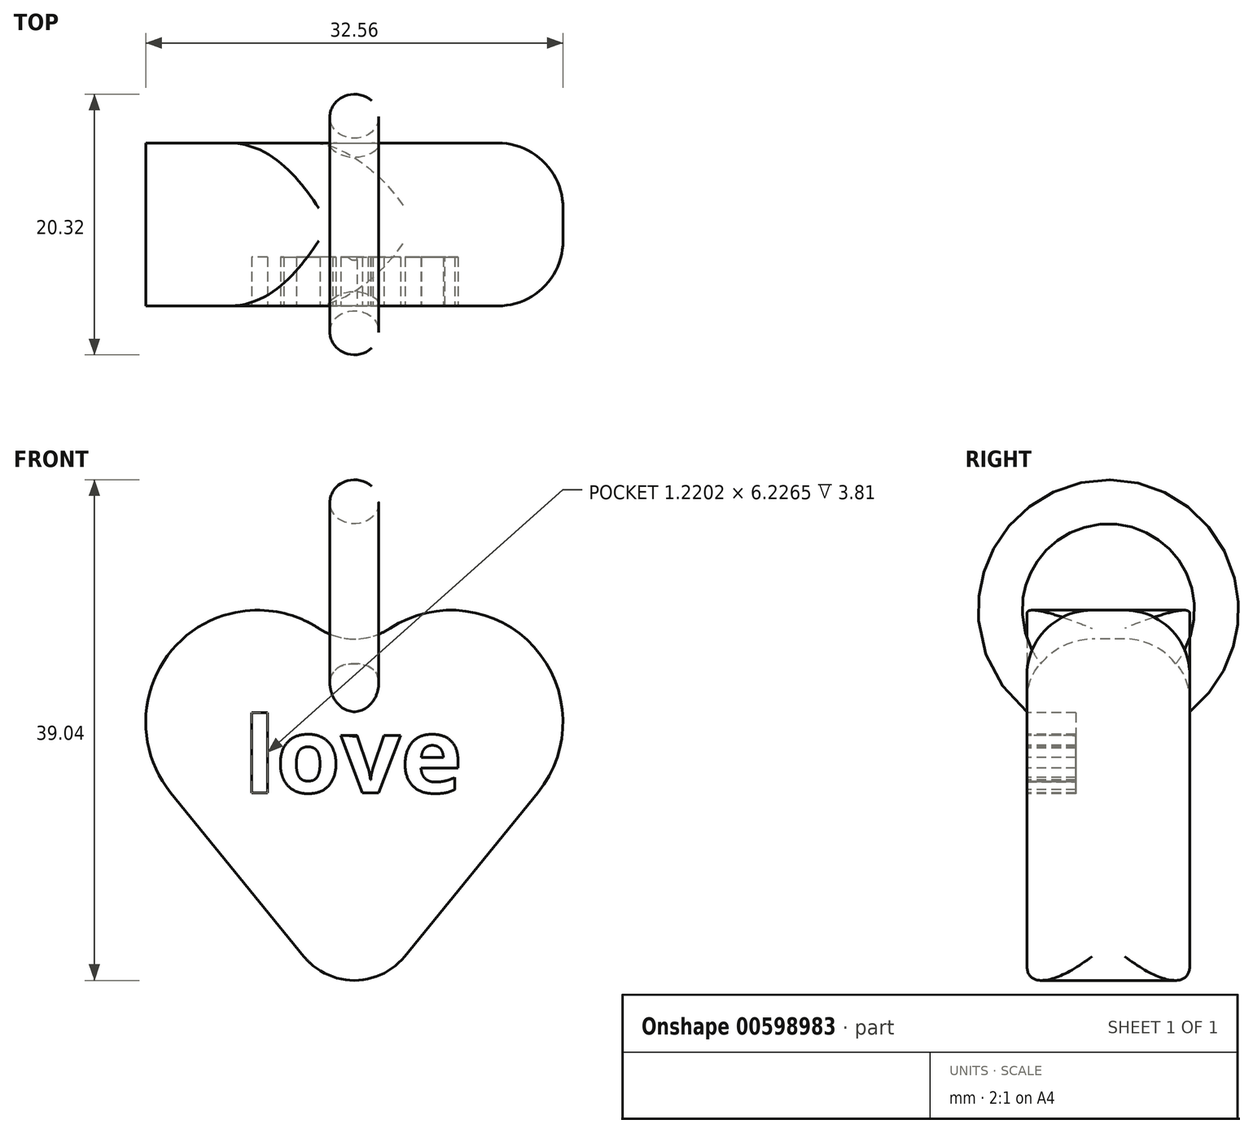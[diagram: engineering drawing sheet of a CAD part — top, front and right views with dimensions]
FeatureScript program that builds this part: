
annotation { "Feature Type Name" : "Feature", "Feature Type Description" : "" }
export const myFeature = defineFeature(function(context is Context, id is Id, definition is map)
    precondition{}
    {
        {
            var Q0;
            Q0=qCreatedBy(makeId("Front.planeOp"),FACE);
            var sketch = newSketch(context, id + "F0", { "sketchPlane" : qUnion([Q0])});
            skLineSegment(sketch, "E0", {"start": v(0, 0) * mm, "end": v(0, -17.62) * mm});
            skLineSegment(sketch, "E1", {"start": v(0, -17.62) * mm, "end": v(14.32, 0) * mm});
            skArc(sketch, "E2", {"start": v(14.32, 0) * mm, "mid": v(12.5, 12.69) * mm, "end": v(0, 9.89) * mm});
            skArc(sketch, "E3.MirrorCS", {"start": v(-14.32, 0) * mm, "mid": v(-12.5, 12.69) * mm, "end": v(0, 9.89) * mm});
            skLineSegment(sketch, "E4.MirrorCS", {"start": v(0, -17.62) * mm, "end": v(-14.32, 0) * mm});
            skSolve(sketch);
        }
        {
            var Q0;
            Q0=makeQuery(id+"F0.imprint","IMPRINT",FACE,{"disambiguationData":[TD([[makeQuery(id+"F0.imprint","IMPRINT",EDGE,{"derivedFrom":sQuery(id+"F0.wireOp",EDGE,"E1")}),1.0]])]});
            extrude(context, id + "F1", {"entities" : qUnion([Q0]), "depth" : 12.7 * mm, "offsetDistance" : 25.4 * mm});
        }
        {
            var Q0;
            Q0=makeQuery(id+"F1.opExtrude","SWEPT_FACE",FACE,{"disambiguationData":[OSD([sQuery(id+"F0.wireOp",EDGE,"E1")])]});
            var Q1;
            Q1=makeQuery(id+"F1.opExtrude","SWEPT_FACE",FACE,{"disambiguationData":[OSD([sQuery(id+"F0.wireOp",EDGE,"E2")])]});
            fillet(context, id + "F2", {"entities" : qUnion([Q0, Q1]), "radius" : 5.08 * mm, "tangentPropagation" : true, "allowEdgeOverflow" : false});
        }
        {
            var Q0;
            Q0=makeQuery(id+"F1.opExtrude","CAP_FACE",FACE,{"disambiguationData":[OSD([sQuery(id+"F0.wireOp",EDGE,"E1"),sQuery(id+"F0.wireOp",EDGE,"E2"),sQuery(id+"F0.wireOp",EDGE,"E3.MirrorCS"),sQuery(id+"F0.wireOp",EDGE,"E4.MirrorCS")])],"isStart":false});
            var sketch = newSketch(context, id + "F3", { "sketchPlane" : qUnion([Q0])});
            skText(sketch, "E5", { "text": "love", "fontName": "OpenSans-Bold.ttf"});
            skPoint(sketch, "E6.0", {"position": v(0, 0) * mm});
            const initialGuessF3  = {"E5": [-0.00864, 0, 1, 0, 0.0059]};
            skSetInitialGuess(sketch, initialGuessF3);
            skSolve(sketch);
        }
        {
            var Q0;
            Q0 = qSketchRegion(id + "F3", true);
            extrude(context, id + "F4", {"entities" : qUnion([Q0]), "operationType" : NewBodyOperationType.REMOVE, "oppositeDirection" : true, "depth" : 3.8 * mm, "offsetDistance" : 25.4 * mm});
        }
        {
            var Q0;
            Q0=qCreatedBy(makeId("Right.planeOp"),FACE);
            var sketch = newSketch(context, id + "F5", { "sketchPlane" : qUnion([Q0])});
            skLineSegment(sketch, "E7", {"start": v(-4.8, 11.99) * mm, "end": v(-7.62, 11.99) * mm});
            skEllipticalArc(sketch, "E8.0.0", {});
            skLineSegment(sketch, "E8.0.1", {"start": v(-7.62, 12.81) * mm, "end": v(-7.62, 11.99) * mm});
            skEllipticalArc(sketch, "E8.0.2", {});
            skLineSegment(sketch, "E8.0.3", {"start": v(-12.7, 8.56) * mm, "end": v(-12.7, 6.9) * mm});
            skArc(sketch, "E9", {"start": v(-0.2, 8.29) * mm, "mid": v(-2.01, 10.96) * mm, "end": v(-5.08, 11.99) * mm});
            skCircle(sketch, "E10", {"center": v(-6.35, 14.25) * mm, "radius": 7.62 * mm});
            skPoint(sketch, "E10.third.point", {"position": v(-1.88, 18.94) * mm});
            skLineSegment(sketch, "E11", {"start": v(-6.21, 11.99) * mm, "end": v(-6.21, 11.99) * mm});
            skPoint(sketch, "E11.endSnap0", {"position": v(-6.21, 11.99) * mm});
            skLineSegment(sketch, "E12", {"start": v(-6.21, 11.99) * mm, "end": v(-6.21, 27.43) * mm, "construction": true});
            const initialGuessF5  = {"E8.0.0": [-0.00762, 0.008559706465169858, -1, 0, 0.00508, 0.004253868776224409, 4.71238898038469, 0], "E8.0.2": [-0.00762, 0.008559706465169858, -1, 0, 0.00508, 0.0042538687762244095, 4.71238898038469, 0]};
            skSetInitialGuess(sketch, initialGuessF5);
            skSolve(sketch);
        }
        {
            var Q0;
            Q0=qCreatedBy(makeId("Top.planeOp"),FACE);
            cPlane(context, id + "F6", {"entities" : qUnion([Q0]), "cplaneType" : CPlaneType.OFFSET, "offset" : 17.78 * mm, "width" : 152.4 * mm, "height" : 152.4 * mm});
        }
        {
            var Q0;
            Q0=qCreatedBy(id+"F6.planeOp",FACE);
            var sketch = newSketch(context, id + "F7", { "sketchPlane" : qUnion([Q0])});
            skLineSegment(sketch, "E13.0", {"start": v(0, 1.27) * mm, "end": v(0, -13.97) * mm});
            skCircle(sketch, "E14", {"center": v(0, -13.97) * mm, "radius": 1.9 * mm});
            skSolve(sketch);
        }
        {
            var Q0;
            Q0=makeQuery(id+"F7.imprint","IMPRINT",FACE,{"disambiguationData":[TD([[makeQuery(id+"F7.imprint","IMPRINT",EDGE,{"derivedFrom":sQuery(id+"F7.wireOp",EDGE,"E14")}),1.0]])]});
            var Q1;
            Q1=sQuery(id+"F5.wireOp",EDGE,"E10");
            sweep(context, id + "F8", {"operationType" : NewBodyOperationType.ADD, "profiles" : qUnion([Q0]), "path" : qUnion([Q1])});
        }
    });
